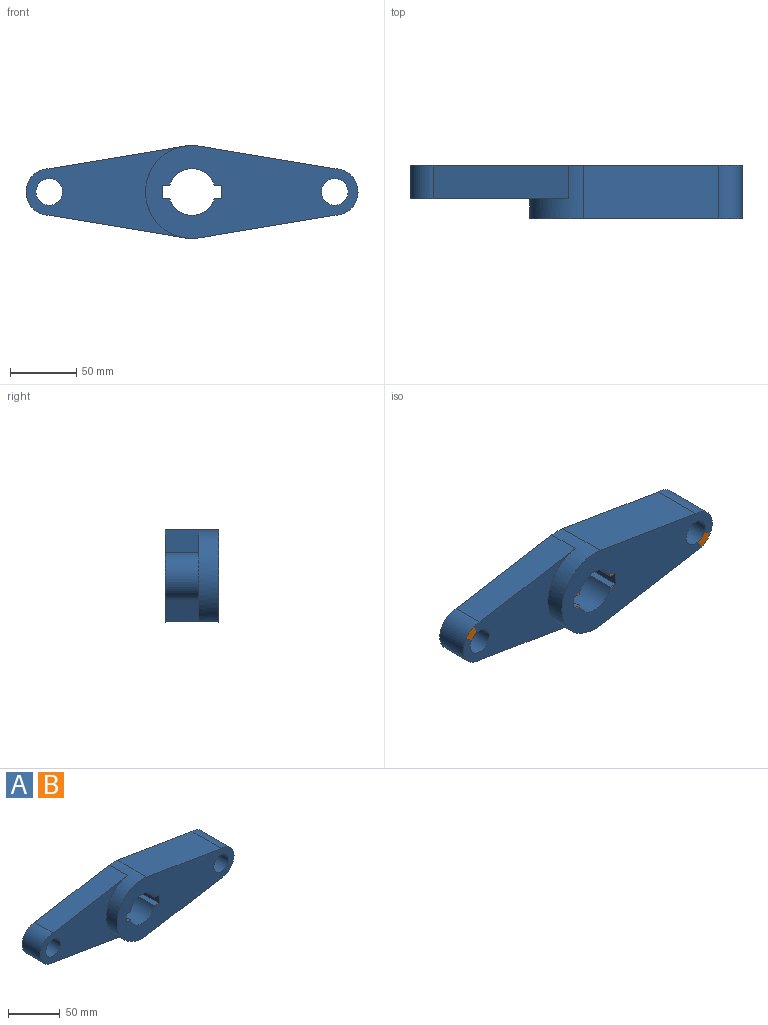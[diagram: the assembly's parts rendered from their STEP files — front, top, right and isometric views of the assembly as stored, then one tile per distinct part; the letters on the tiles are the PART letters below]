
ASSEMBLY  parts=2 mates=2
PART A: 20 faces, bbox 250x40x70 mm
  f0: cylinder r=35mm len=70mm, axis (0,1,0), area 2403.6mm2, adj f1,f10,f13,f14,f15,f17,f19
  f1: plane 101.72x40mm, normal (0.17,0,-0.99), area 4125.5mm2, adj f0,f2,f13,f14
  f2: cylinder r=17.5mm len=40mm, axis (0,1,0), area 2199.1mm2, adj f1,f10,f13,f14
  f3: cylinder r=17.5mm len=40mm, axis (0,1,0), area 1793.5mm2, adj f4,f11,f13,f14
  f4: plane 40x5.73mm, normal (0,0,1), area 229.2mm2, adj f3,f5,f13,f14
  f5: plane 40x10mm, normal (1,0,0), area 400mm2, adj f4,f6,f13,f14
  f6: plane 40x5.73mm, normal (0,0,-1), area 229.2mm2, adj f5,f7,f13,f14
  f7: cylinder r=17.5mm len=40mm, axis (0,1,0), area 1793.5mm2, adj f6,f8,f13,f14
  f8: plane 40x5.73mm, normal (0,0,-1), area 229.2mm2, adj f7,f9,f13,f14
  f9: plane 40x10mm, normal (-1,0,0), area 400mm2, adj f8,f11,f13,f14
  f10: plane 101.72x40mm, normal (0.17,0,0.99), area 4125.5mm2, adj f0,f2,f13,f14
  f11: plane 40x5.73mm, normal (0,0,1), area 229.2mm2, adj f3,f9,f13,f14
  f12: cylinder r=10mm len=40mm, axis (0,1,0), area 2513.3mm2, adj f13,f14
  f13: plane 160x70mm, normal (0,-1,0), area 6718.4mm2, adj f0,f1,f2,f3,f4,f5,f6,f7
  f14: plane 250x70mm, normal (0,1,0), area 10655.2mm2, adj f0,f1,f2,f3,f4,f5,f6,f7
  f15: plane 101.72x25mm, normal (-0.17,0,0.99), area 2578.5mm2, adj f0,f14,f16,f19
  f16: cylinder r=17.5mm len=35mm, axis (0,1,0), area 1374.4mm2, adj f14,f15,f17,f19
  f17: plane 101.72x25mm, normal (-0.17,0,-0.99), area 2578.5mm2, adj f0,f14,f16,f19
  f18: cylinder r=10mm len=25mm, axis (0,1,0), area 1570.8mm2, adj f14,f19
  f19: plane 119.22x69.04mm, normal (0,-1,0), area 3936.8mm2, adj f0,f15,f16,f17,f18
PART B: same geometry as A
PLACE A t=(-89.5,5.34,-24.08)mm
PLACE B t=(-89.5,5.34,-24.08)mm
MATE revolute B.f12 <-> A.f12  axis (0,1,0) through (18,5.34,-24.08)mm
MATE parallel A.f13 <-> B.f14  axis (0,-1,0) through (-50.13,-34.66,-24.08)mm
